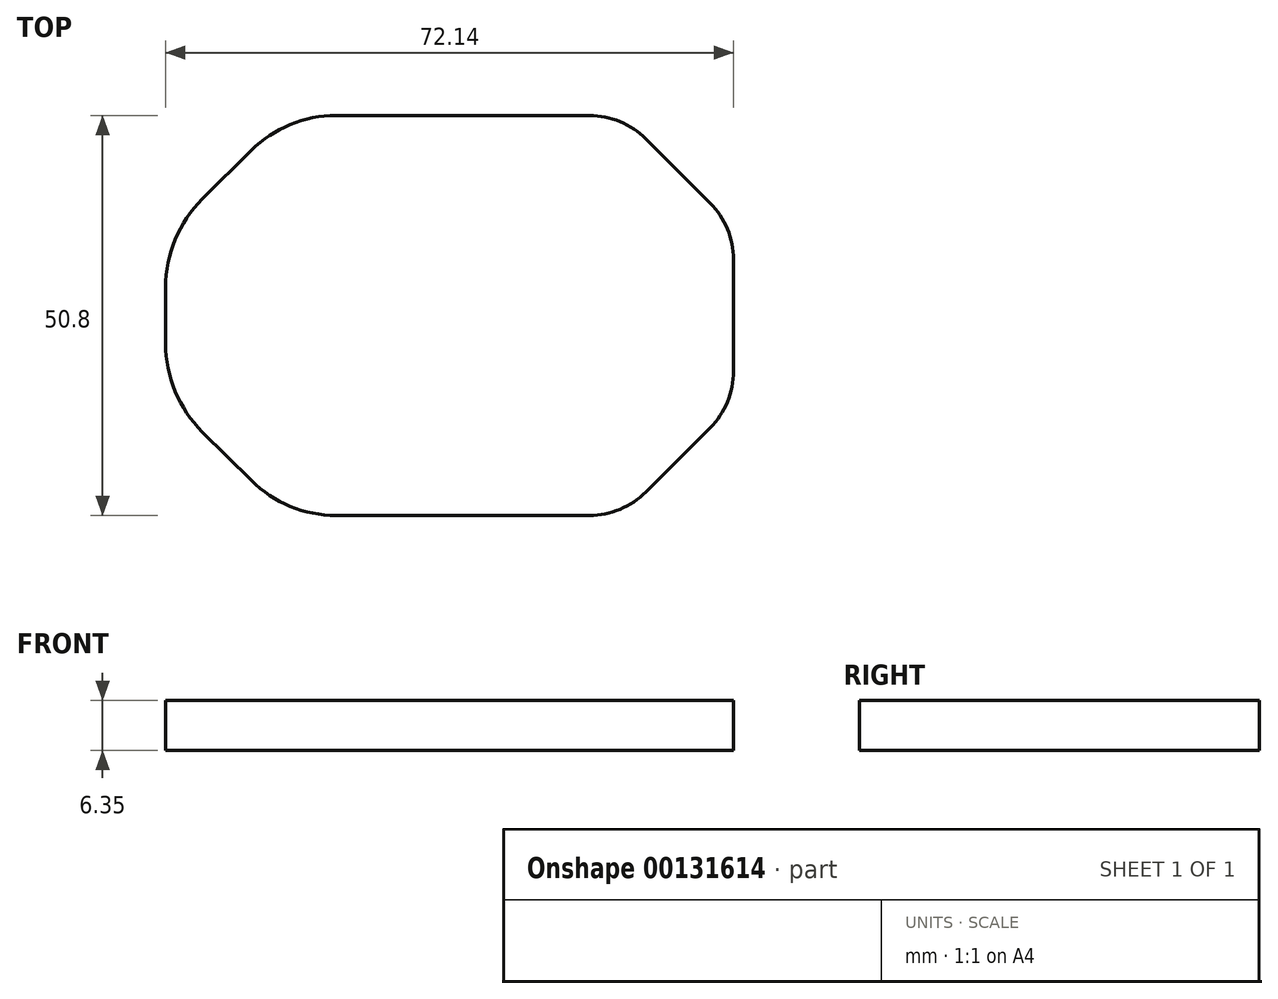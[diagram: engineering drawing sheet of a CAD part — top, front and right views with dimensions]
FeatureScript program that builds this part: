
annotation { "Feature Type Name" : "Feature", "Feature Type Description" : "" }
export const myFeature = defineFeature(function(context is Context, id is Id, definition is map)
    precondition{}
    {
        {
            var Q0;
            Q0=qCreatedBy(makeId("Top.planeOp"),FACE);
            var sketch = newSketch(context, id + "F0", { "sketchPlane" : qUnion([Q0])});
            skLineSegment(sketch, "E0.bottom", {"start": v(0, 20.4) * mm, "end": v(0, 34.59) * mm});
            skLineSegment(sketch, "E0.top", {"start": v(-72.14, 23.9) * mm, "end": v(-72.14, 31.1) * mm});
            skLineSegment(sketch, "E0.left", {"start": v(-18.3, 2.1) * mm, "end": v(-50.5, 2.1) * mm});
            skLineSegment(sketch, "E0.right", {"start": v(-18.3, 52.9) * mm, "end": v(-50.5, 52.9) * mm});
            skLineSegment(sketch, "E1", {"start": v(-11.12, 5.07) * mm, "end": v(-2.98, 13.21) * mm});
            skArc(sketch, "E2.filletArc", {"start": v(-18.3, 2.1) * mm, "mid": v(-14.42, 2.87) * mm, "end": v(-11.12, 5.07) * mm});
            skArc(sketch, "E3.filletArc", {"start": v(-2.98, 13.21) * mm, "mid": v(-0.77, 16.5) * mm, "end": v(0, 20.4) * mm});
            skArc(sketch, "E4.MirrorCS", {"start": v(-18.3, 52.9) * mm, "mid": v(-14.42, 52.12) * mm, "end": v(-11.12, 49.92) * mm});
            skLineSegment(sketch, "E5.MirrorCS", {"start": v(-11.12, 49.92) * mm, "end": v(-2.98, 41.77) * mm});
            skArc(sketch, "E6.MirrorCS", {"start": v(-2.98, 41.77) * mm, "mid": v(-0.77, 38.47) * mm, "end": v(0, 34.59) * mm});
            skLineSegment(sketch, "E7", {"start": v(-61.22, 6.51) * mm, "end": v(-67.48, 12.71) * mm});
            skArc(sketch, "E8.filletArc", {"start": v(-61.22, 6.51) * mm, "mid": v(-56.3, 3.24) * mm, "end": v(-50.5, 2.1) * mm});
            skArc(sketch, "E9.filletArc", {"start": v(-72.14, 23.9) * mm, "mid": v(-70.92, 17.84) * mm, "end": v(-67.48, 12.71) * mm});
            skArc(sketch, "E10.MirrorCS", {"start": v(-61.22, 48.47) * mm, "mid": v(-56.3, 51.74) * mm, "end": v(-50.5, 52.9) * mm});
            skLineSegment(sketch, "E11.MirrorCS", {"start": v(-61.22, 48.47) * mm, "end": v(-67.48, 42.27) * mm});
            skArc(sketch, "E12.MirrorCS", {"start": v(-72.14, 31.1) * mm, "mid": v(-70.92, 37.15) * mm, "end": v(-67.48, 42.27) * mm});
            skSolve(sketch);
        }
        {
            var Q0;
            Q0 = qSketchRegion(id + "F0", true);
            extrude(context, id + "F1", {"entities" : qUnion([Q0]), "depth" : 6.35 * mm});
        }
    });
